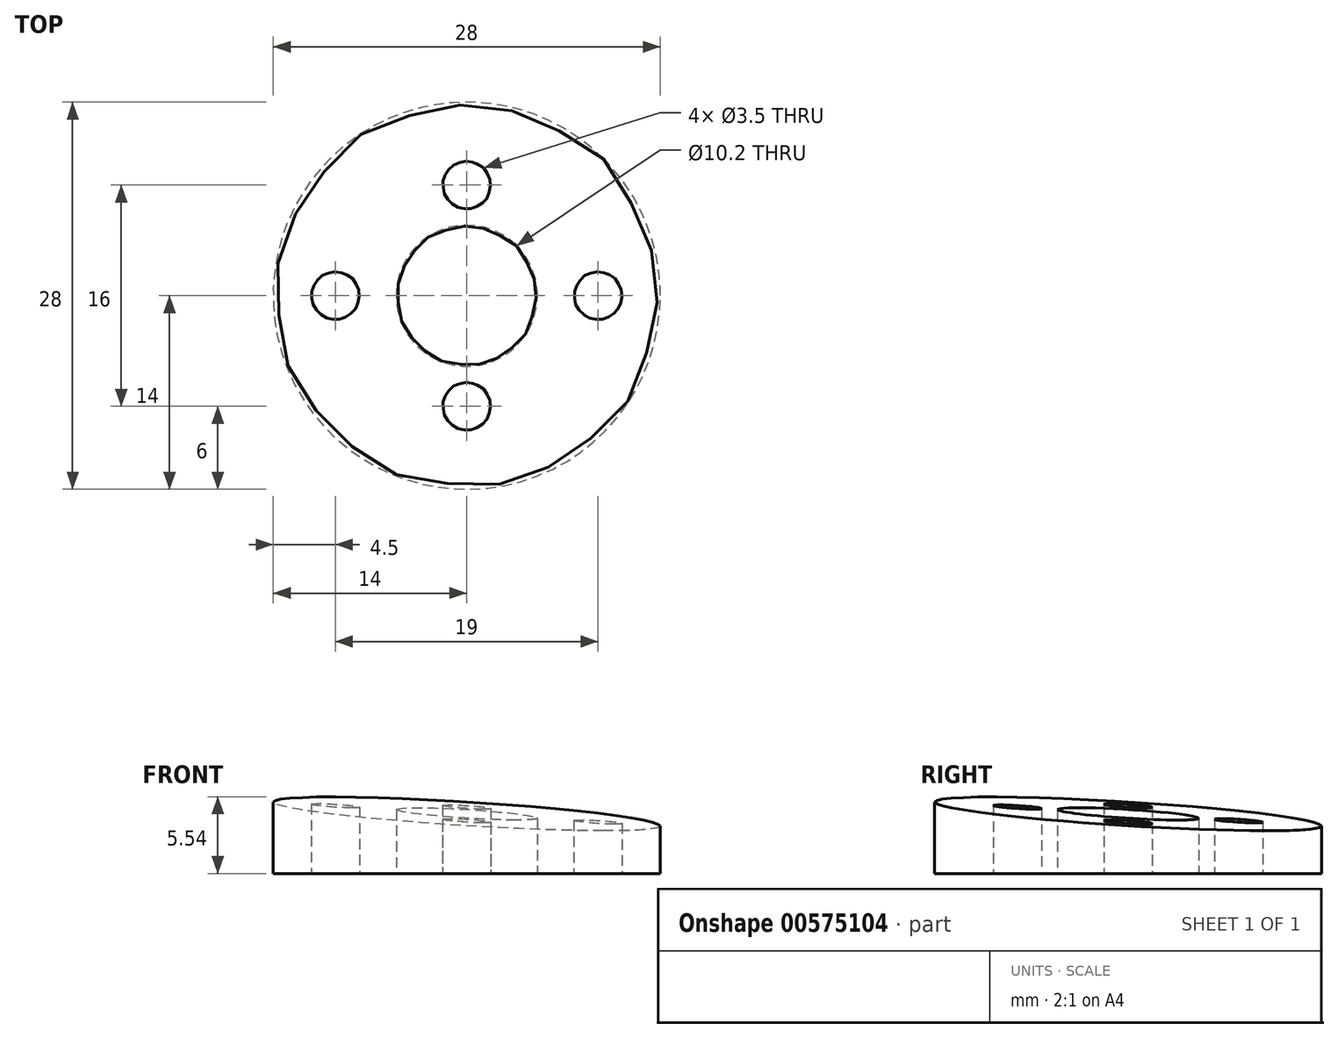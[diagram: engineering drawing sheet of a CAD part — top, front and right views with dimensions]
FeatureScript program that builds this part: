
annotation { "Feature Type Name" : "Feature", "Feature Type Description" : "" }
export const myFeature = defineFeature(function(context is Context, id is Id, definition is map)
    precondition{}
    {
        {
            var Q0;
            Q0=qCreatedBy(makeId("Top.planeOp"),FACE);
            var sketch = newSketch(context, id + "F0", { "sketchPlane" : qUnion([Q0])});
            skCircle(sketch, "E0", {"center": v(0, 0) * mm, "radius": 14 * mm});
            skCircle(sketch, "E1", {"center": v(0, 0) * mm, "radius": 8 * mm, "construction": true});
            skCircle(sketch, "E2", {"center": v(0, 0) * mm, "radius": 9.5 * mm, "construction": true});
            skCircle(sketch, "E3", {"center": v(0, 8) * mm, "radius": 1.75 * mm});
            skCircle(sketch, "E4", {"center": v(0, -8) * mm, "radius": 1.75 * mm});
            skCircle(sketch, "E5", {"center": v(-9.5, 0) * mm, "radius": 1.75 * mm});
            skCircle(sketch, "E6", {"center": v(9.5, 0) * mm, "radius": 1.75 * mm});
            skCircle(sketch, "E7", {"center": v(0, 0) * mm, "radius": 5.1 * mm});
            skSolve(sketch);
        }
        {
            var Q0;
            Q0 = qSketchRegion(id + "F0", true);
            extrude(context, id + "F1", {"entities" : qUnion([Q0]), "depth" : 10 * mm, "offsetDistance" : 25 * mm});
        }
        {
            var Q0;
            Q0=qCreatedBy(makeId("Top.planeOp"),FACE);
            var sketch = newSketch(context, id + "F2", { "sketchPlane" : qUnion([Q0])});
            skLineSegment(sketch, "E8", {"start": v(30.34, 30.34) * mm, "end": v(-30.72, -30.72) * mm, "construction": true});
            skLineSegment(sketch, "E9", {"start": v(0, 0) * mm, "end": v(26.2, -26.2) * mm, "construction": true});
            skSolve(sketch);
        }
        {
            var Q0;
            Q0=sQuery(id+"F2.wireOp",EDGE,"E8");
            cPlane(context, id + "F3", {"entities" : qUnion([Q0]), "cplaneType" : CPlaneType.LINE_ANGLE, "offset" : 25 * mm, "angle" : 90 * degree, "width" : 150 * mm, "height" : 150 * mm});
        }
        {
            var Q0;
            Q0=qCreatedBy(id+"F3.planeOp",FACE);
            cPlane(context, id + "F4", {"entities" : qUnion([Q0]), "cplaneType" : CPlaneType.OFFSET, "offset" : 25 * mm, "width" : 150 * mm, "height" : 150 * mm});
        }
        {
            var Q0;
            Q0=qCreatedBy(id+"F4.planeOp",FACE);
            var sketch = newSketch(context, id + "F5", { "sketchPlane" : qUnion([Q0])});
            skLineSegment(sketch, "E10", {"start": v(-15, 0) * mm, "end": v(15, 0) * mm});
            skLineSegment(sketch, "E11", {"start": v(15, 0) * mm, "end": v(15, 3) * mm});
            skLineSegment(sketch, "E12", {"start": v(15, 3) * mm, "end": v(-15, 5.62) * mm});
            skLineSegment(sketch, "E13", {"start": v(-15, 5.62) * mm, "end": v(-15, 0) * mm});
            skLineSegment(sketch, "E14", {"start": v(15, 0) * mm, "end": v(15, -3) * mm});
            skLineSegment(sketch, "E15", {"start": v(15, -3) * mm, "end": v(-15, -3) * mm});
            skLineSegment(sketch, "E16", {"start": v(-15, -3) * mm, "end": v(-15, 0) * mm});
            skPoint(sketch, "E17", {"position": v(0, 0) * mm});
            skSolve(sketch);
        }
        {
            var Q0;
            Q0 = qSketchRegion(id + "F5", true);
            extrude(context, id + "F6", {"entities" : qUnion([Q0]), "operationType" : NewBodyOperationType.INTERSECT, "oppositeDirection" : true, "depth" : 40 * mm, "offsetDistance" : 25 * mm});
        }
    });
